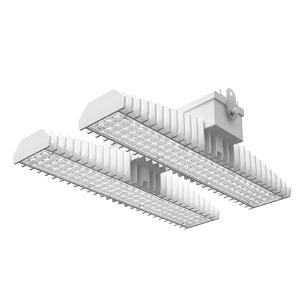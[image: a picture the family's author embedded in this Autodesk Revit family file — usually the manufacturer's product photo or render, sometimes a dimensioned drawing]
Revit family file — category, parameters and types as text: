
# Revit family: 3f_filippi_-_3f_lem_concentrato_3f_filippi_-_58888_a0811_-_3f_lem_2_led_100_cr_conc___vt_1065
name_source: partatom
category: Lighting Fixtures
units: mm (PartAtom-declared; Revit-internal decimal feet)

## family parameters
Cut with Voids When Loaded = No
Host = Face
Light Source = No
Part Type = Normal
Room Calculation Point = No
Round Connector Dimension = Use Diameter
Shared = No

## types (1)
- 3F Filippi - 3F LEM Concentrato (1 x LED, 15155 lm, 109 W, 4000 K)
    Apparent Load = 109 VA
    Approval mark = CE
    CIE Flux Codes = 83 96 99 100 100
    Color Rendering = 80
    Color Temperature = 4000 K
    Control Gear = Electronic ballast
    Default Elevation = 1800 mm
    Description = Industrial luminaire with high light output and high luminous efficiency designed with the most innovative technologies for environments with temperature up to 55°C.

ILLUMINOTECHNICAL
Luminous efficiency 100% (DLOR 99%, ULOR 1%).
Initial luminous flux of the luminaire 15155 lm.
Direct symmetric narrow distribution: the illuminated area has a elliptical shape.
Installation Interdistance Transv.D = 0.52 x hu - Long.D = 1.16 x hu.
Tabular UGR (CIE 117 - 4H-8H; S=0.25H; 70/50/20): RUG 16.4 - 20.3.
Beam angle: 31° - 73°.
Luminous efficacy 139 lm/W.
Lifetime (L93/B10): 30000 h. (tq+25°C)
Lifetime (L90/B10): 50000 h. (tq+25°C)
Lifetime (L85/B10): 80000 h. (tq+25°C)
Lifetime (L80/B10): 100000 h. (tq+25°C)
Lifetime (L85/B10): 50000 h. (tq+55°C)
Sudden decreased luminous flux after 50000 hours: 0% (C0).
Photobiological safety in compliance with IEC/TR 62778: RG0 risk exempt, (IEC 62471).
In compliance with IEC/EN 62722-2-1 - IEC/EN 62717 standards.

SOURCE
2 Mid-Power linear LED modules 50W/840.
Energy efficiency class (UE 2019/2020 - UE 2019/2015): C.
CIE 13.3 Colour rendering index: CRI >80 (R9 <50%).
IES TM-30 Fidelity Index: Rf = 84 Rg = 95.
CCT nominal colour temperature 4000 K.
Colour initial tolerance (MacAdam): SDCM 3.

MECHANICAL
Passive modular heatsinks in die-casted aluminium, painted in white colour.
To optimize the thermal management of the LED module, the heatsinks are oversized and provided with self-cleaning of cooling fins.
Wiring body in aluminium and galvanised steel anchored solidly to the sinks and thermally separated.
3F Lens lenses with high luminous efficiency, transparent methacrylate (PMMA), fixed to the LED modules.
Fixing brackets in stainless steel.
Luminaire with limited surface temperature. - D - (EN 60598-2-24)
Dimensions: 470x542 mm, height 133 mm. Weight 10.084 kg.
IP65 protection degree.
Mechanical strength to impacts IK06 (1 joule).
Glow-wire test resistance 650°C.

ELECTRICAL
Halogen Free electronic wiring 230V-50/60Hz, power factor 0.97, THD <25%, constant output current, class I, 1 driver.
Power of the luminaire 109 W.
ENEC - CE.
SAFE FLICKER: PstLM=<1 and SVM=<0.4 (IEC TR 61547-1 and IEC TR 63158), to ensure a more comfortable and safe light.
Luminaire compliant with EN 60598-2-22 for power supply from a centralised emergency system CPSS (Central Power Supply System), not incorporated in the luminaire - high risk areas excluded. The default power and flux are 100% in AC and 100% in DC.
Ambient temperature from -30°C to +55°C.
Temperature class T6 max 85°C.
Quick connection via M20 3P connector with 9-13 mm tightening range.
Power unit positioned on a separate compartment by the LED module to ensure optimum temperatures of cabling components, to be inspectable and maintainable.
Relative humidity UR: <85%.

INSTALLATION
Ceiling / Suspended / Wall.
All accessories dedicated to this product are available on the Catalog and on our website www.3F-Filippi.com.

ACCESSORIES
A0811 - VT transparent glass, tempered, not flammable, with sealing gasket.
One required for each light module. The pack contains 10 pieces.

APPLICATIONS
In commercial environments, exhibition and industrial areas, stores, open areas.
Applications with high ambient temperature up to 55°C.
Environments in which it is necessary a total protection against falling fragments (eg environments with foodstuffs or machines with moving parts or with extreme temperature changes), use luminaires with polycarbonate lenses.

WARNING
Fixture not suitable for cold stores with an ambient temperature <0°C and/or relative humidity >85%.
Luminaire designed for disposal/recycling at end-of-life.
Replaceable (LED only) light source by a professional. Replaceable control gear by a professional.
    Height = 133 mm  [stored 0.436352 ft]
    Lamp = 1 x LED
    Lamp Light Flux = 15155 lm
    Lamp Power = 109 W
    Lamp count = 1
    Length = 470 mm
    Lifetime = 50000 h
    Luminous efficacy = 139 lm/W
    Manufacturer = 3F Filippi
    ModVariant = No
    Model = 3F Filippi - 58888+A0811 - 3F LEM 2 LED 100 CR CONC + VT
    Mounting Place = Ceiling
    Mounting Type = Pendant
    Number of Poles = 1
    OnlyDefault = Yes
    Power Factor = 1
    Product Name = 3F Filippi - 3F LEM Concentrato
    Product group = pendant luminaire
    ProductGroupID = 9
    Protection Class = Protection class I
    Protection Degree = IP 65
    RLX_Detail_Level = 1
    RLX_Emergency_Light_Flux = 0 lm
    RLX_Emergency_Type = 0
    RLX_Emergency_Type_DB = No
    RlxData = <blob elided: 102741 chars, md5=78e72fbe>
    Socket = socket
    Standby Power = 0 W
    System Light Flux = 15155 lm
    System Power = 109 W
    Type Comments = Product without accessories
    Type Image = 3f_filippi_-_lem_2__a0811.jpg
    URL = http://relux.com
    VarID = ---
    Voltage = 0 V
    Weight = 0.00 kg
    Width = 542 mm

note: [stored X ft] marks values corroborated as IEEE doubles in the binary element streams (Revit-internal decimal feet)

## geometry (parser evidence)
native form markers: Blend x4, Sweep x13
no freeform markers — native parametric forms only
